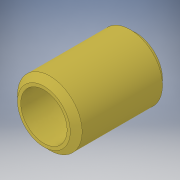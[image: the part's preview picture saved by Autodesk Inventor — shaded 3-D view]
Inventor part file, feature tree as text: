
AUTODESK INVENTOR PART (.ipt)
format: ipt  version: 2019 (Build 230136000, 136)  size: 132,608 bytes
history: native  units: in
note: dims shown in document units (in); Inventor stores cm internally (conversion verified against a paired STEP export)
features: other x35, revolve x1, sketch x1
ambient origin geometry x8: Origin, YZ Plane, XZ Plane, XY Plane, X Axis, Y Axis, Z Axis, Center Point
bodies: Solid1 (feature_tree)
feature tree (37):
  revolve  "Revolution1"  [1 undecoded]
  other  "bushing_XY"
  other  "bushing_YZ"
  other  "bushing_ZX"
  other  "bushing_X"
  other  "bushing_Y"
  other  "bushing_Z"
  other  "bushing_Center"
  other  "id1_XY"
  other  "id1_YZ"
  other  "id1_ZX"
  other  "id1_X"
  other  "id1_Y"
  other  "id1_Z"
  other  "id1_Center"
  other  "id2_XY"
  other  "id2_YZ"
  other  "id2_ZX"
  other  "id2_X"
  other  "id2_Y"
  other  "id2_Z"
  other  "id2_Center"
  other  "id3_XY"
  other  "id3_YZ"
  other  "id3_ZX"
  other  "id3_X"
  other  "id3_Y"
  other  "id3_Z"
  other  "id3_Center"
  other  "id4_XY"
  other  "id4_YZ"
  other  "id4_ZX"
  other  "id4_X"
  other  "id4_Y"
  other  "id4_Z"
  other  "id4_Center"
  sketch  "Sketch_1"  dims[d0=360.0deg d1=0.0in d2=0.0in]
note: 1 required parameter value undecoded (feature->parameter linkage not recoverable at this tier; creation-order binding heuristic only, values carry confidence <= 0.55)
